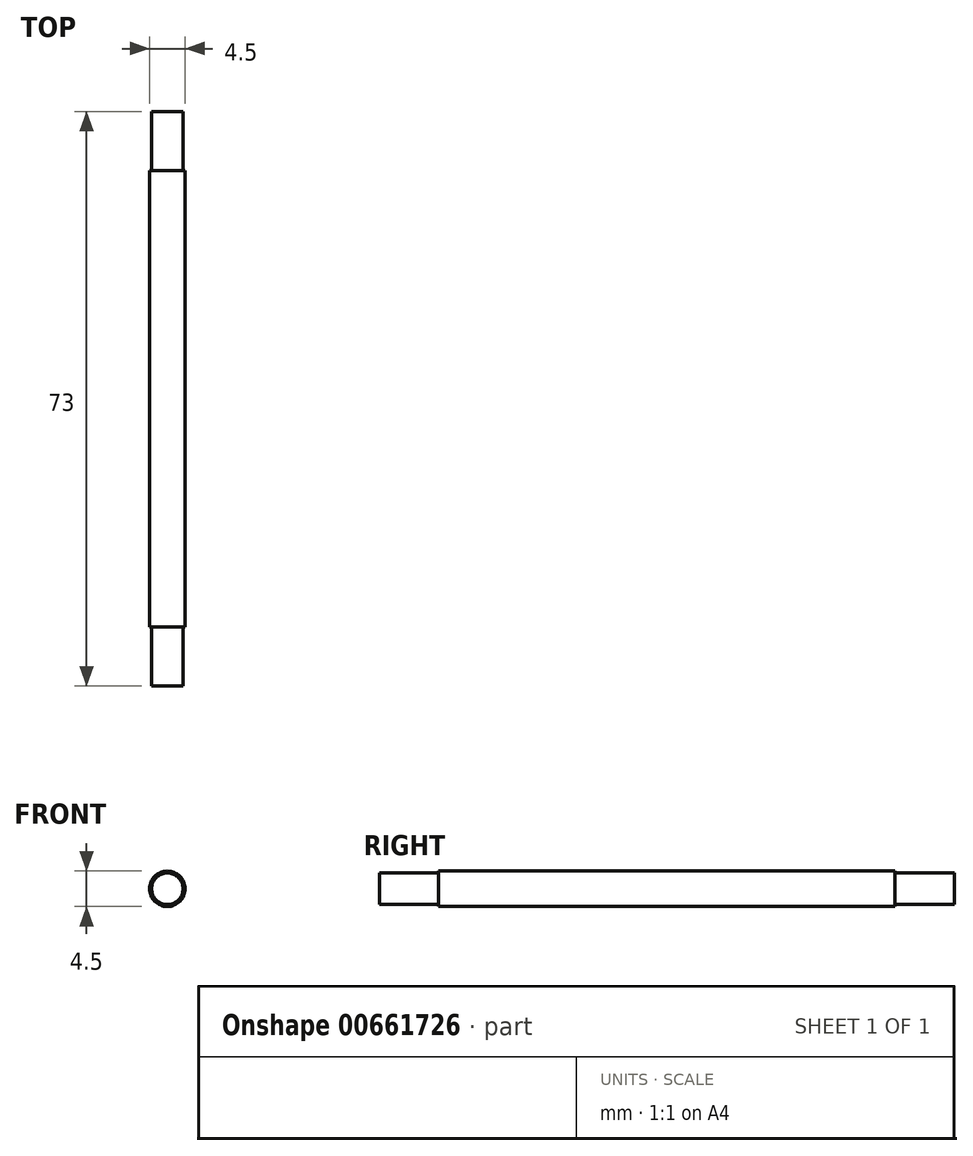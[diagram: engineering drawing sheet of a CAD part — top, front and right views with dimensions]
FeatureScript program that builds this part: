
annotation { "Feature Type Name" : "Feature", "Feature Type Description" : "" }
export const myFeature = defineFeature(function(context is Context, id is Id, definition is map)
    precondition{}
    {
        {
            var Q0;
            Q0=qCreatedBy(makeId("Front.planeOp"),FACE);
            var sketch = newSketch(context, id + "F0", { "sketchPlane" : qUnion([Q0])});
            skCircle(sketch, "E0", {"center": v(0, 0) * mm, "radius": 2 * mm});
            skSolve(sketch);
        }
        {
            var Q0;
            Q0 = qSketchRegion(id + "F0", true);
            extrude(context, id + "F1", {"entities" : qUnion([Q0]), "depth" : 7.5 * mm, "offsetDistance" : 25 * mm});
        }
        {
            var Q0;
            Q0=makeQuery(id+"F1.opExtrude","CAP_FACE",FACE,{"disambiguationData":[OSD([sQuery(id+"F0.wireOp",EDGE,"E0")])],"isStart":false});
            var sketch = newSketch(context, id + "F2", { "sketchPlane" : qUnion([Q0])});
            skCircle(sketch, "E1", {"center": v(0, 0) * mm, "radius": 2.25 * mm});
            skSolve(sketch);
        }
        {
            var Q0;
            Q0=makeQuery(id+"F2.imprint","IMPRINT",FACE,{"disambiguationData":[TD([[makeQuery(id+"F2.imprint","IMPRINT",EDGE,{"derivedFrom":sQuery(id+"F2.wireOp",EDGE,"E1")}),1.0]])]});
            var Q1;
            Q1=makeQuery(id+"F2.imprint","IMPRINT",FACE,{"disambiguationData":[TD([[makeQuery(id+"F2.imprint","IMPRINT",EDGE,{"derivedFrom":makeQuery(id+"F1.opExtrude","CAP_EDGE",EDGE,{"disambiguationData":[OSD([sQuery(id+"F0.wireOp",EDGE,"E0")])],"isStart":false})}),1.0]])]});
            extrude(context, id + "F3", {"entities" : qUnion([Q0, Q1]), "operationType" : NewBodyOperationType.ADD, "depth" : 58 * mm, "offsetDistance" : 25 * mm});
        }
        {
            var Q0;
            Q0=makeQuery(id+"F3.opExtrude","CAP_FACE",FACE,{"disambiguationData":[OSD([sQuery(id+"F2.wireOp",EDGE,"E1")])],"isStart":false});
            var sketch = newSketch(context, id + "F4", { "sketchPlane" : qUnion([Q0])});
            skCircle(sketch, "E2", {"center": v(0, 0) * mm, "radius": 2 * mm});
            skSolve(sketch);
        }
        {
            var Q0;
            Q0 = qSketchRegion(id + "F4", true);
            extrude(context, id + "F5", {"entities" : qUnion([Q0]), "operationType" : NewBodyOperationType.ADD, "depth" : 7.5 * mm, "offsetDistance" : 25 * mm});
        }
    });
